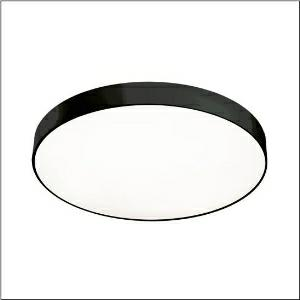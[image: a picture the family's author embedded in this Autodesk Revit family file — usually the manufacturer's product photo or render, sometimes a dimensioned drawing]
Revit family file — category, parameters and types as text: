
# Revit family: round_21_l_51mr38fd0321b
name_source: partatom
category: Lighting Fixtures
units: mm (PartAtom-declared; Revit-internal decimal feet)

## family parameters
Cut with Voids When Loaded = No
Host = Face
Light Source = No
Part Type = Normal
Room Calculation Point = No
Round Connector Dimension = Use Diameter
Shared = No

## types (1)
- Round 21 L (1 x LED, 13590 lm, 97 W, 3000K)
    Apparent Load = 97 VA
    CIE Flux Codes = 49 80 96 100 100
    Color Rendering = 80
    Color Temperature = 3000K
    Default Elevation = 1800 mm
    Description = Round 21 L, wall and ceiling luminaire, primary optical cover: cover, of PMMA, opal, light emission: direct distribution, primary light characteristic: symmetric, installation type: suspended mounting, surface-mounted, LED, rated luminous flux: 13.590lm, luminous efficacy: 140lm/W, light colour: 830, colour temperature: 3000K, control gear: DALI 2, with terminal, 5-pole, mains connection: 230V, AC, 50/60Hz, rated input power: 97W, housing, of aluminium, coated, black, diameter: 850mm, height: 62mm, protection rating (complete): IP40, insulation class (complete): insulation class I (protective earthing), certification: CE, impact resistance: IK04, permissible operating ambient temperature: -10..+35°C, packaging unit: 1 piece
    Height = 87 mm
    Lamp = 1 x LED
    Lamp Light Flux = 13590 lm
    Lamp Power = 97 W
    Lamp count = 1
    Length = 850 mm
    Luminous efficacy = 140 lm/W
    Manufacturer = Siteco
    ModVariant = No
    Model = 51MR38FD0321B
    Mounting Place = Ceiling
    Mounting Type = Surface mounted
    Number of Poles = 1
    OnlyDefault = Yes
    Power Factor = 1
    Product Name = Round 21 L
    Product group = wall and ceiling luminaire
    ProductGroupID = 304
    Protection Class = Protection class I
    Protection Degree = IP 40
    RLX_Detail_Level = 1
    RLX_Emergency_Light_Flux = 0 lm
    RLX_Emergency_Type = 0
    RLX_Emergency_Type_DB = No
    RlxData = <blob elided: 23901 chars, md5=d143d230>
    Socket = socket
    Standby Power = 0 W
    System Light Flux = 13590 lm
    System Power = 97 W
    Type Comments = Product without accessories
    Type Image = l_1258328.jpg
    URL = http://relux.com
    VarID = ---
    Voltage = 0 V
    Weight = 0.00 kg
    Width = 0 mm  [stored 0 ft]

note: [stored X ft] marks values corroborated as IEEE doubles in the binary element streams (Revit-internal decimal feet)

## geometry (parser evidence)
native form markers: Blend x4, Sweep x12
no freeform markers — native parametric forms only
